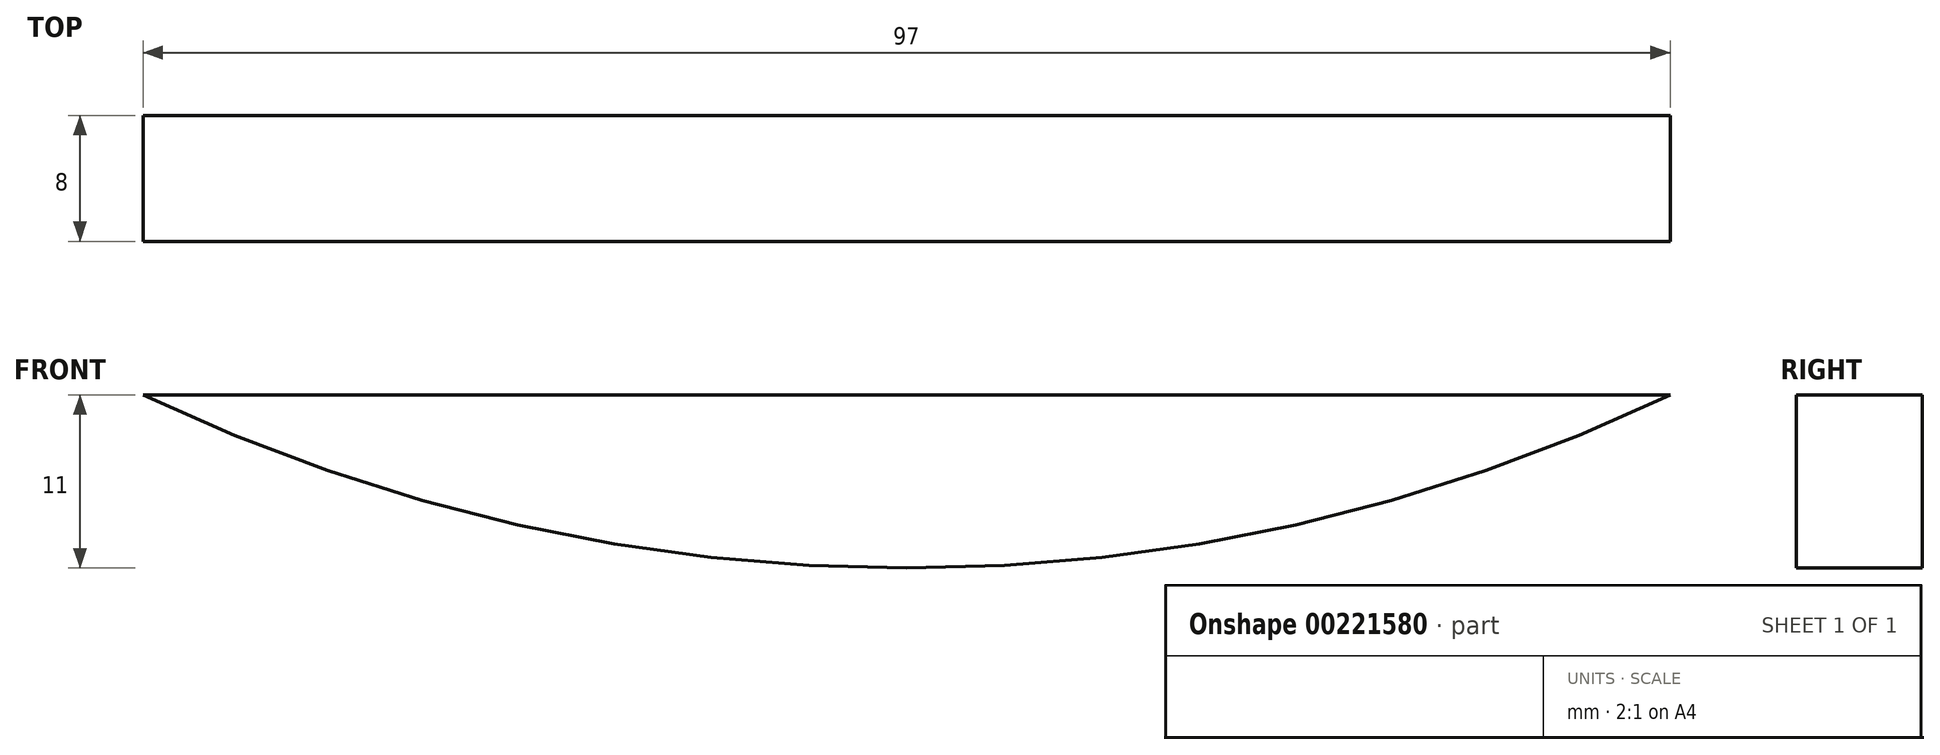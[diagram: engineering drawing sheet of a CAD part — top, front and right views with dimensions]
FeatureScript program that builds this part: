
annotation { "Feature Type Name" : "Feature", "Feature Type Description" : "" }
export const myFeature = defineFeature(function(context is Context, id is Id, definition is map)
    precondition{}
    {
        {
            var Q0;
            Q0=qCreatedBy(makeId("Front.planeOp"),FACE);
            var sketch = newSketch(context, id + "F0", { "sketchPlane" : qUnion([Q0])});
            skLineSegment(sketch, "E0", {"start": v(-44.66, 23.8) * mm, "end": v(52.34, 23.8) * mm});
            skArc(sketch, "E1", {"start": v(-44.66, 23.8) * mm, "mid": v(3.84, 12.8) * mm, "end": v(52.34, 23.8) * mm});
            skSolve(sketch);
        }
        {
            var Q0;
            Q0=makeQuery(id+"F0.imprint","IMPRINT",FACE,{"disambiguationData":[TD([[makeQuery(id+"F0.imprint","IMPRINT",EDGE,{"derivedFrom":sQuery(id+"F0.wireOp",EDGE,"E0")}),-1.0]])]});
            extrude(context, id + "F1", {"entities" : qUnion([Q0]), "depth" : 8 * mm});
        }
    });
